# Revit family: Sanitary_Taps-Mixers_Gala_Grecia-Dual-tap-shower-mixer
name_source: partatom
category: Plumbing Fixtures
units: mm (PartAtom-declared; Revit-internal decimal feet)

## family parameters
Always vertical = No
Cut with Voids When Loaded = No
OmniClass Number = 23.45.00.00
OmniClass Title = Sanitary, Laundry, and Cleaning Equipment
Part Type = Normal
Room Calculation Point = No
Round Connector Dimension = Use Diameter
Shared = No
Work Plane-Based = Yes

## types (1)
- Grecia Dual tap shower mixer
    BIMobject category = Taps & Mixers
    BIMobject category code = sanitary-taps-mixers
    BIMobject main category = Sanitary
    BIMobject main category code = sanitary
    BOSUseNativeGeometries = 1
    Brand url = http://gala.es
    Default Elevation = 1219 mm
    Design country = Spain
    Edition number = 1
    IFC Classification = Sanitary Terminal
    Installation instructions = https://www.gala.es
    Manufacturer country = Spain
    Manufacturer name = Gala
    Masterformat 2014 Code = 22 41 39
    Masterformat 2014 Description = Residential Faucets, Supplies, and Trim
    Material main = Chrome
    NBS Reference Code = 55-70-40
    NBS Reference Description = Hot And Cold Water Supply Systems
    OmniClass Code = 23-31 11 00
    OmniClass Description = Faucets
    Product Guid = 2dc19a97-1646-4388-ba6b-40f28e9597b1
    Product SKU = 3897200
    Product data url = https://bimobject.com
    Product family = Grecia
    Product group = Tap Fittings
    Product name = Grecia Dual tap shower mixer
    Product url = https://www.gala.es
    QR code = http://bimobject.com
    Technical description = https://www.gala.es
    UNSPSC Code = 3018
    Uniclass 1.4 Code = L725111
    Uniclass 1.4 Description = Mixer taps
    Uniclass 2.0 Code = SS-55-70-40
    Uniclass 2.0 Description = Hot And Cold Water Supply Systems
    Uniclass 2015 Code = Pr_40_20_87
    Uniclass 2015 Name = Taps and water supply outlet fittings
    Uniformat II Code = D2010
    Uniformat II Description = Plumbing Fixtures

## geometry (parser evidence)
native form markers: Sweep x2
no freeform markers — native parametric forms only
